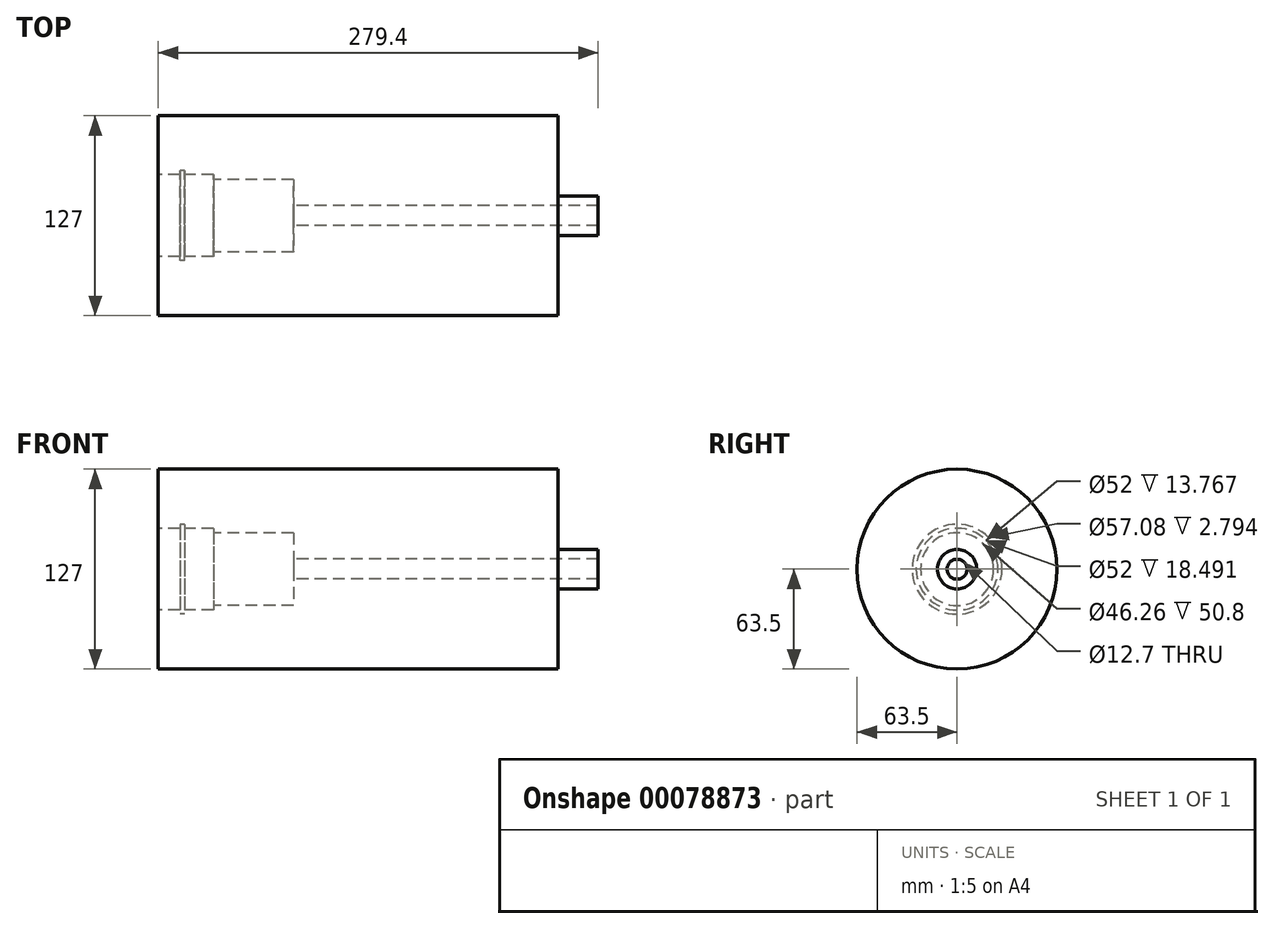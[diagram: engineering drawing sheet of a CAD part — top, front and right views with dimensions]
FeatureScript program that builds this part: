
annotation { "Feature Type Name" : "Feature", "Feature Type Description" : "" }
export const myFeature = defineFeature(function(context is Context, id is Id, definition is map)
    precondition{}
    {
        {
            var Q0;
            Q0=qCreatedBy(makeId("Front.planeOp"),FACE);
            var sketch = newSketch(context, id + "F0", { "sketchPlane" : qUnion([Q0])});
            skLineSegment(sketch, "E0", {"start": v(0, 63.5) * mm, "end": v(0, 26) * mm});
            skLineSegment(sketch, "E1", {"start": v(0, 26) * mm, "end": v(13.77, 26) * mm});
            skLineSegment(sketch, "E2", {"start": v(13.77, 26) * mm, "end": v(13.77, 28.54) * mm});
            skLineSegment(sketch, "E3", {"start": v(13.77, 28.54) * mm, "end": v(16.56, 28.54) * mm});
            skLineSegment(sketch, "E4", {"start": v(16.56, 28.54) * mm, "end": v(16.56, 26) * mm});
            skLineSegment(sketch, "E5", {"start": v(16.56, 26) * mm, "end": v(35.05, 26) * mm});
            skLineSegment(sketch, "E6", {"start": v(35.05, 26) * mm, "end": v(35.05, 23.13) * mm});
            skLineSegment(sketch, "E7", {"start": v(35.05, 23.13) * mm, "end": v(85.85, 23.13) * mm});
            skLineSegment(sketch, "E8", {"start": v(85.85, 23.13) * mm, "end": v(85.85, 6.35) * mm});
            skLineSegment(sketch, "E9", {"start": v(85.85, 6.35) * mm, "end": v(279.4, 6.35) * mm});
            skLineSegment(sketch, "E10", {"start": v(279.4, 6.35) * mm, "end": v(279.4, 12.5) * mm});
            skLineSegment(sketch, "E11", {"start": v(279.4, 12.5) * mm, "end": v(254, 12.5) * mm});
            skLineSegment(sketch, "E12", {"start": v(254, 12.5) * mm, "end": v(254, 63.5) * mm});
            skLineSegment(sketch, "E13", {"start": v(254, 63.5) * mm, "end": v(0, 63.5) * mm});
            skLineSegment(sketch, "E14", {"start": v(0, 0) * mm, "end": v(45.27, 0) * mm, "construction": true});
            skSolve(sketch);
        }
        {
            var Q0;
            Q0=makeQuery(id+"F0.imprint","IMPRINT",FACE,{"disambiguationData":[TD([[makeQuery(id+"F0.imprint","IMPRINT",EDGE,{"derivedFrom":sQuery(id+"F0.wireOp",EDGE,"E0")}),1.0]])]});
            var Q1;
            Q1=sQuery(id+"F0.wireOp",EDGE,"E14");
            revolve(context, id + "F1", {"entities" : qUnion([Q0]), "axis" : qUnion([Q1]), "revolveType" : RevolveType.FULL});
        }
    });
